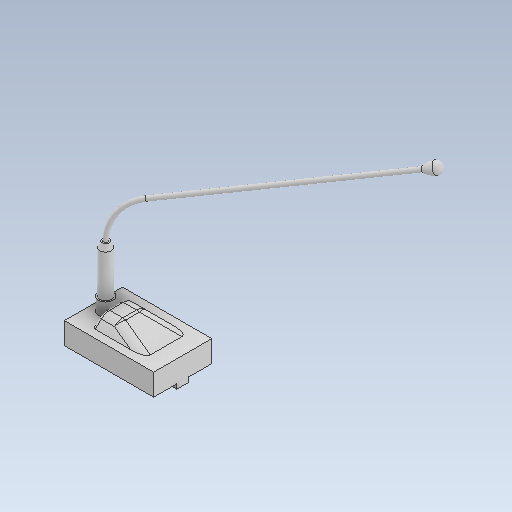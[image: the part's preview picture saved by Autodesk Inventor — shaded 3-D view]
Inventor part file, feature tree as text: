
AUTODESK INVENTOR PART (.ipt)
format: ipt  version: 2021 (Build 250183000, 183)  size: 177,664 bytes
history: native  units: mm
features: sketch x10, other x6, plane x1
ambient origin geometry x8: Origin, YZ Plane, XZ Plane, XY Plane, X Axis, Y Axis, Z Axis, Center Point
bodies: Body1 (feature_tree), Body2 (feature_tree)
feature tree (17):
  other  "準確無線麥克風組.ipt"
  other  "實體1::準確無線麥克風組.ipt"
  other  "標籤特徵1"
  sketch  "草圖1"
  sketch  "草圖2"
  sketch  "草圖3"
  sketch  "草圖4"
  sketch  "草圖5"
  sketch  "草圖6"
  sketch  "草圖7"
  sketch  "草圖8"
  sketch  "草圖9"
  sketch  "草圖10"
  plane  "工作平面1"
  other  "Srf1"
  other  "實體1"
  other  "Srf1::導出"
